annotation { "Feature Type Name" : "Feature", "Feature Type Description" : "" }
export const myFeature = defineFeature(function(context is Context, id is Id, definition is map)
    precondition{}
    {
        {
            var Q0;
            Q0=qCreatedBy(makeId("Front.planeOp"),FACE);
            var sketch = newSketch(context, id + "F0", { "sketchPlane" : qUnion([Q0])});
            skLineSegment(sketch, "E0.bottom", {"start": v(-49, -0.15) * mm, "end": v(61, -0.15) * mm});
            skLineSegment(sketch, "E0.top", {"start": v(-49, -30.15) * mm, "end": v(61, -30.15) * mm});
            skLineSegment(sketch, "E0.left", {"start": v(-49, -0.15) * mm, "end": v(-49, -30.15) * mm});
            skLineSegment(sketch, "E0.right", {"start": v(61, -0.15) * mm, "end": v(61, -30.15) * mm});
            skSolve(sketch);
        }
        {
            var Q0;
            Q0 = qSketchRegion(id + "F0", true);
            var Q1;
            Q1=makeQuery(id+"F0.imprint","IMPRINT",FACE,{"disambiguationData":[TD([[makeQuery(id+"F0.imprint","IMPRINT",EDGE,{"derivedFrom":sQuery(id+"F0.wireOp",EDGE,"E0.bottom")}),-1.0]])]});
            extrude(context, id + "F1", {"entities" : qUnion([Q0, Q1]), "depth" : 25 * mm, "offsetDistance" : 25 * mm});
        }
        {
            var Q0;
            Q0=makeQuery(id+"F1.opExtrude","SWEPT_FACE",FACE,{"disambiguationData":[OSD([sQuery(id+"F0.wireOp",EDGE,"E0.right")])]});
            var sketch = newSketch(context, id + "F2", { "sketchPlane" : qUnion([Q0])});
            skLineSegment(sketch, "E1", {"start": v(-25, -0.15) * mm, "end": v(-25, -25.15) * mm});
            skLineSegment(sketch, "E2", {"start": v(-25, -25.15) * mm, "end": v(-5, -25.15) * mm});
            skLineSegment(sketch, "E3", {"start": v(-5, -25.15) * mm, "end": v(-25, -0.15) * mm});
            skLineSegment(sketch, "E4", {"start": v(-5, -25.15) * mm, "end": v(0, -25.15) * mm});
            skLineSegment(sketch, "E5", {"start": v(0, -25.15) * mm, "end": v(-20, -0.15) * mm});
            skLineSegment(sketch, "E6", {"start": v(-20, -0.15) * mm, "end": v(0, -0.15) * mm});
            skLineSegment(sketch, "E7", {"start": v(0, -0.15) * mm, "end": v(0, -25.15) * mm});
            skSolve(sketch);
        }
        {
            var Q0;
            Q0 = qSketchRegion(id + "F2", true);
            extrude(context, id + "F3", {"entities" : qUnion([Q0]), "operationType" : NewBodyOperationType.REMOVE, "oppositeDirection" : true, "depth" : 115 * mm, "offsetDistance" : 25 * mm});
        }
        {
            var Q0;
            Q0=makeQuery(id+"F3.boolean.opBoolean","COPY",FACE,{"derivedFrom":makeQuery(id+"F3.opExtrude","SWEPT_FACE",FACE,{"disambiguationData":[OSD([sQuery(id+"F2.wireOp",EDGE,"E5")])]})});
            var sketch = newSketch(context, id + "F4", { "sketchPlane" : qUnion([Q0])});
            skLineSegment(sketch, "E8", {"start": v(-61, 12.38) * mm, "end": v(-61, -19.64) * mm});
            skSolve(sketch);
        }
        {
            var Q0;
            Q0=makeQuery(id+"F3.boolean.opBoolean","COPY",FACE,{"derivedFrom":makeQuery(id+"F3.opExtrude","SWEPT_FACE",FACE,{"disambiguationData":[OSD([sQuery(id+"F2.wireOp",EDGE,"E5")])]})});
            var sketch = newSketch(context, id + "F5", { "sketchPlane" : qUnion([Q0])});
            skText(sketch, "E9", { "text": "Joshua Williamson", "fontName": "OpenSans-Bold.ttf"});
            skText(sketch, "E10", { "text": "Professional GNU Emacs User", "fontName": "OpenSans-Italic.ttf"});
            const initialGuessF5  = {"E9": [-0.0585, -0.0008, 1, 0, 0.00819], "E10": [-0.0585, -0.01464, 1, 0, 0.00575]};
            skSetInitialGuess(sketch, initialGuessF5);
            skSolve(sketch);
        }
        {
            var Q0;
            Q0 = qSketchRegion(id + "F5", true);
            extrude(context, id + "F6", {"entities" : qUnion([Q0]), "operationType" : NewBodyOperationType.ADD, "depth" : 1 * mm, "offsetDistance" : 25 * mm});
        }
    });